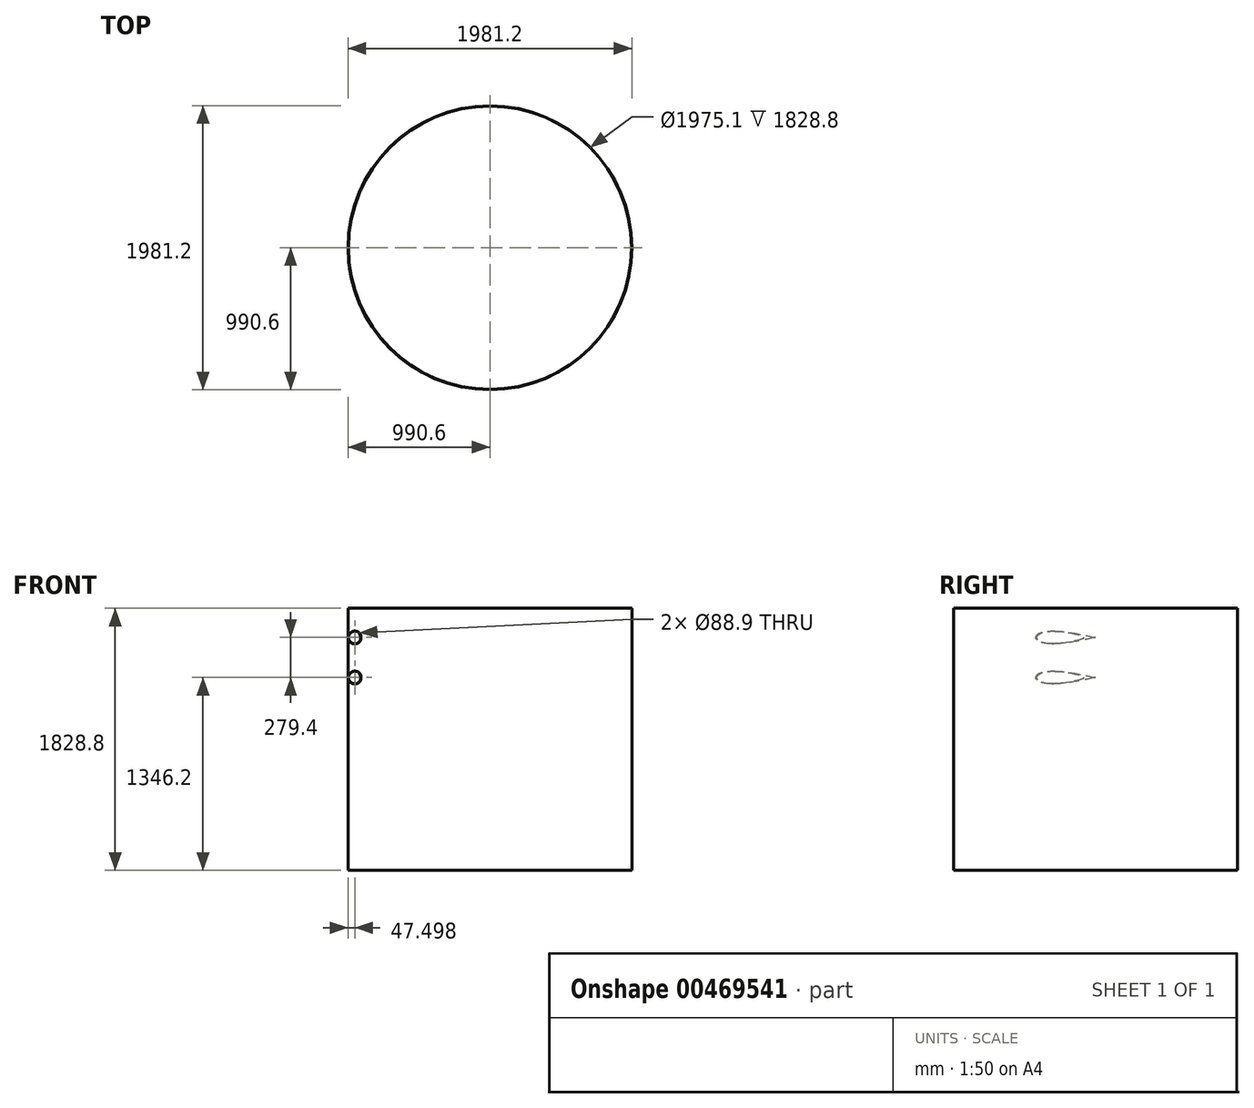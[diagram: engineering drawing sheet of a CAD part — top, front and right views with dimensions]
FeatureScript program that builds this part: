
annotation { "Feature Type Name" : "Feature", "Feature Type Description" : "" }
export const myFeature = defineFeature(function(context is Context, id is Id, definition is map)
    precondition{}
    {
        {
            var Q0;
            Q0=qCreatedBy(makeId("Top.planeOp"),FACE);
            var sketch = newSketch(context, id + "F0", { "sketchPlane" : qUnion([Q0])});
            skCircle(sketch, "E0", {"center": v(0, 0) * mm, "radius": 990.6 * mm});
            skCircle(sketch, "E1", {"center": v(0, 0) * mm, "radius": 987.55 * mm});
            skSolve(sketch);
        }
        {
            var Q0;
            Q0 = qSketchRegion(id + "F0", true);
            extrude(context, id + "F1", {"entities" : qUnion([Q0]), "depth" : 1828.8 * mm, "offsetDistance" : 25.4 * mm});
        }
        {
            var Q0;
            Q0=qCreatedBy(makeId("Front.planeOp"),FACE);
            var sketch = newSketch(context, id + "F2", { "sketchPlane" : qUnion([Q0])});
            skCircle(sketch, "E2", {"center": v(-943.1, 1625.6) * mm, "radius": 44.45 * mm});
            skCircle(sketch, "E3", {"center": v(-943.1, 1346.2) * mm, "radius": 44.45 * mm});
            skLineSegment(sketch, "E4", {"start": v(-990.6, 0) * mm, "end": v(-990.6, 1828.8) * mm, "construction": true});
            skSolve(sketch);
        }
        {
            var Q0;
            Q0 = qSketchRegion(id + "F2", true);
            extrude(context, id + "F3", {"entities" : qUnion([Q0]), "operationType" : NewBodyOperationType.REMOVE, "endBound" : BoundingType.THROUGH_ALL, "depth" : 25.4 * mm, "offsetDistance" : 25.4 * mm});
        }
    });
